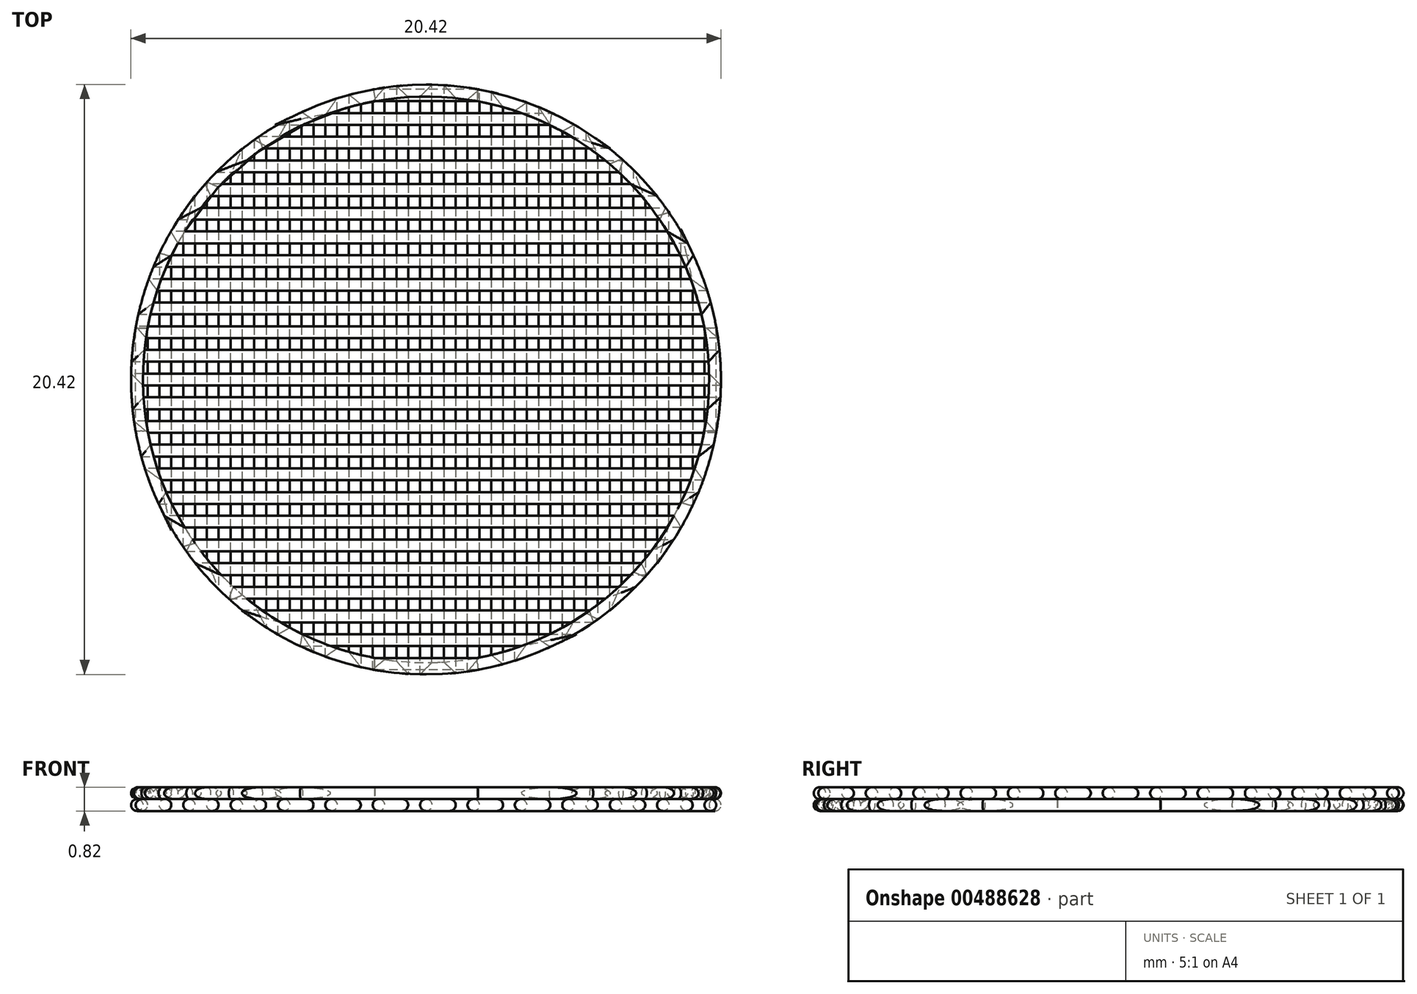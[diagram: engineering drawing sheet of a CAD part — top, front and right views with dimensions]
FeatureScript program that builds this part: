
annotation { "Feature Type Name" : "Feature", "Feature Type Description" : "" }
export const myFeature = defineFeature(function(context is Context, id is Id, definition is map)
    precondition{}
    {
        {
            assignVariable(context, id + "F0", {"name" : "d", "anyValue" : 0.4 * mm});
        }
        {
            var Q0;
            Q0=qCreatedBy(makeId("Top.planeOp"),FACE);
            cPlane(context, id + "F1", {"entities" : qUnion([Q0]), "cplaneType" : CPlaneType.OFFSET, "offset" : getVariable(context, 'd') / 2, "width" : 150 * mm, "height" : 150 * mm});
        }
        {
            var Q0;
            Q0=qCreatedBy(id+"F1.planeOp",FACE);
            var sketch = newSketch(context, id + "F2", { "sketchPlane" : qUnion([Q0])});
            skLineSegment(sketch, "E0.bottom", {"start": v(10, 10) * mm, "end": v(-10, 10) * mm});
            skLineSegment(sketch, "E0.top", {"start": v(10, -10) * mm, "end": v(-10, -10) * mm});
            skLineSegment(sketch, "E0.left", {"start": v(10, 10) * mm, "end": v(10, -10) * mm});
            skLineSegment(sketch, "E0.right", {"start": v(-10, 10) * mm, "end": v(-10, -10) * mm});
            skPoint(sketch, "E0.middle", {"position": v(0, 0) * mm});
            skLineSegment(sketch, "E1", {"start": v(10, -10) * mm, "end": v(9.84, -10) * mm});
            skLineSegment(sketch, "E2", {"start": v(9.84, -10) * mm, "end": v(9.02, -10) * mm});
            skLineSegment(sketch, "E3", {"start": v(9.02, -10) * mm, "end": v(8.2, -10) * mm});
            skLineSegment(sketch, "E4", {"start": v(8.2, -10) * mm, "end": v(7.38, -10) * mm});
            skLineSegment(sketch, "E5", {"start": v(7.38, -10) * mm, "end": v(6.56, -10) * mm});
            skLineSegment(sketch, "E6", {"start": v(6.56, -10) * mm, "end": v(5.74, -10) * mm});
            skLineSegment(sketch, "E7", {"start": v(5.74, -10) * mm, "end": v(4.92, -10) * mm});
            skLineSegment(sketch, "E8", {"start": v(4.92, -10) * mm, "end": v(4.1, -10) * mm});
            skLineSegment(sketch, "E9", {"start": v(4.1, -10) * mm, "end": v(3.28, -10) * mm});
            skLineSegment(sketch, "E10", {"start": v(3.28, -10) * mm, "end": v(2.46, -10) * mm});
            skLineSegment(sketch, "E11", {"start": v(2.46, -10) * mm, "end": v(1.64, -10) * mm});
            skLineSegment(sketch, "E12", {"start": v(1.64, -10) * mm, "end": v(0.82, -10) * mm});
            skLineSegment(sketch, "E13", {"start": v(0.82, -10) * mm, "end": v(0, -10) * mm});
            skLineSegment(sketch, "E14", {"start": v(0, -10) * mm, "end": v(-0.82, -10) * mm});
            skLineSegment(sketch, "E15", {"start": v(-0.82, -10) * mm, "end": v(-1.64, -10) * mm});
            skLineSegment(sketch, "E16", {"start": v(-1.64, -10) * mm, "end": v(-2.46, -10) * mm});
            skLineSegment(sketch, "E17", {"start": v(-2.46, -10) * mm, "end": v(-3.28, -10) * mm});
            skLineSegment(sketch, "E18", {"start": v(-3.28, -10) * mm, "end": v(-4.1, -10) * mm});
            skLineSegment(sketch, "E19", {"start": v(-4.1, -10) * mm, "end": v(-4.92, -10) * mm});
            skLineSegment(sketch, "E20", {"start": v(-4.92, -10) * mm, "end": v(-5.74, -10) * mm});
            skLineSegment(sketch, "E21", {"start": v(-5.74, -10) * mm, "end": v(-6.56, -10) * mm});
            skLineSegment(sketch, "E22", {"start": v(-6.56, -10) * mm, "end": v(-7.38, -10) * mm});
            skLineSegment(sketch, "E23", {"start": v(-7.38, -10) * mm, "end": v(-8.2, -10) * mm});
            skLineSegment(sketch, "E24", {"start": v(-8.2, -10) * mm, "end": v(-9.02, -10) * mm});
            skLineSegment(sketch, "E25", {"start": v(-9.02, -10) * mm, "end": v(-9.84, -10) * mm});
            skLineSegment(sketch, "E26", {"start": v(-9.84, -10) * mm, "end": v(-10, -10) * mm});
            skLineSegment(sketch, "E27", {"start": v(9.84, -10) * mm, "end": v(9.84, -1.78) * mm});
            skLineSegment(sketch, "E28", {"start": v(9.84, -1.78) * mm, "end": v(9.84, 1.78) * mm});
            skLineSegment(sketch, "E29", {"start": v(9.84, 1.78) * mm, "end": v(9.84, 10) * mm});
            skLineSegment(sketch, "E30", {"start": v(9.84, 10) * mm, "end": v(10, 10) * mm});
            skLineSegment(sketch, "E31", {"start": v(9.02, -10) * mm, "end": v(9.02, -4.32) * mm});
            skLineSegment(sketch, "E32", {"start": v(9.02, -4.32) * mm, "end": v(9.02, 4.32) * mm});
            skLineSegment(sketch, "E33", {"start": v(9.02, 4.32) * mm, "end": v(9.02, 10) * mm});
            skLineSegment(sketch, "E34", {"start": v(9.02, 10) * mm, "end": v(9.84, 10) * mm});
            skLineSegment(sketch, "E35", {"start": v(8.2, -10) * mm, "end": v(8.2, -5.72) * mm});
            skLineSegment(sketch, "E36", {"start": v(8.2, -5.72) * mm, "end": v(8.2, 5.72) * mm});
            skLineSegment(sketch, "E37", {"start": v(8.2, 5.72) * mm, "end": v(8.2, 10) * mm});
            skLineSegment(sketch, "E38", {"start": v(8.2, 10) * mm, "end": v(9.02, 10) * mm});
            skLineSegment(sketch, "E39", {"start": v(7.38, -10) * mm, "end": v(7.38, -6.75) * mm});
            skLineSegment(sketch, "E40", {"start": v(7.38, -6.75) * mm, "end": v(7.38, 6.75) * mm});
            skLineSegment(sketch, "E41", {"start": v(7.38, 6.75) * mm, "end": v(7.38, 10) * mm});
            skLineSegment(sketch, "E42", {"start": v(7.38, 10) * mm, "end": v(8.2, 10) * mm});
            skLineSegment(sketch, "E43", {"start": v(6.56, -10) * mm, "end": v(6.56, -7.55) * mm});
            skLineSegment(sketch, "E44", {"start": v(6.56, -7.55) * mm, "end": v(6.56, 7.55) * mm});
            skLineSegment(sketch, "E45", {"start": v(6.56, 7.55) * mm, "end": v(6.56, 10) * mm});
            skLineSegment(sketch, "E46", {"start": v(6.56, 10) * mm, "end": v(7.38, 10) * mm});
            skLineSegment(sketch, "E47", {"start": v(5.74, -10) * mm, "end": v(5.74, -8.19) * mm});
            skLineSegment(sketch, "E48", {"start": v(5.74, -8.19) * mm, "end": v(5.74, 8.19) * mm});
            skLineSegment(sketch, "E49", {"start": v(5.74, 8.19) * mm, "end": v(5.74, 10) * mm});
            skLineSegment(sketch, "E50", {"start": v(5.74, 10) * mm, "end": v(6.56, 10) * mm});
            skLineSegment(sketch, "E51", {"start": v(4.92, -10) * mm, "end": v(4.92, -8.7) * mm});
            skLineSegment(sketch, "E52", {"start": v(4.92, -8.7) * mm, "end": v(4.92, 8.7) * mm});
            skLineSegment(sketch, "E53", {"start": v(4.92, 8.7) * mm, "end": v(4.92, 10) * mm});
            skLineSegment(sketch, "E54", {"start": v(4.92, 10) * mm, "end": v(5.74, 10) * mm});
            skLineSegment(sketch, "E55", {"start": v(4.1, -10) * mm, "end": v(4.1, -9.12) * mm});
            skLineSegment(sketch, "E56", {"start": v(4.1, -9.12) * mm, "end": v(4.1, 9.12) * mm});
            skLineSegment(sketch, "E57", {"start": v(4.1, 9.12) * mm, "end": v(4.1, 10) * mm});
            skLineSegment(sketch, "E58", {"start": v(4.1, 10) * mm, "end": v(4.92, 10) * mm});
            skLineSegment(sketch, "E59", {"start": v(3.28, -10) * mm, "end": v(3.28, -9.45) * mm});
            skLineSegment(sketch, "E60", {"start": v(3.28, -9.45) * mm, "end": v(3.28, 9.45) * mm});
            skLineSegment(sketch, "E61", {"start": v(3.28, 9.45) * mm, "end": v(3.28, 10) * mm});
            skLineSegment(sketch, "E62", {"start": v(3.28, 10) * mm, "end": v(4.1, 10) * mm});
            skLineSegment(sketch, "E63", {"start": v(2.46, -10) * mm, "end": v(2.46, -9.7) * mm});
            skLineSegment(sketch, "E64", {"start": v(2.46, -9.7) * mm, "end": v(2.46, 9.7) * mm});
            skLineSegment(sketch, "E65", {"start": v(2.46, 9.7) * mm, "end": v(2.46, 10) * mm});
            skLineSegment(sketch, "E66", {"start": v(2.46, 10) * mm, "end": v(3.28, 10) * mm});
            skLineSegment(sketch, "E67", {"start": v(1.64, -10) * mm, "end": v(1.64, -9.86) * mm});
            skLineSegment(sketch, "E68", {"start": v(1.64, -9.86) * mm, "end": v(1.64, 9.86) * mm});
            skLineSegment(sketch, "E69", {"start": v(1.64, 9.86) * mm, "end": v(1.64, 10) * mm});
            skLineSegment(sketch, "E70", {"start": v(1.64, 10) * mm, "end": v(2.46, 10) * mm});
            skLineSegment(sketch, "E71", {"start": v(0.82, -10) * mm, "end": v(0.82, -9.97) * mm});
            skLineSegment(sketch, "E72", {"start": v(0.82, -9.97) * mm, "end": v(0.82, 9.97) * mm});
            skLineSegment(sketch, "E73", {"start": v(0.82, 9.97) * mm, "end": v(0.82, 10) * mm});
            skLineSegment(sketch, "E74", {"start": v(0.82, 10) * mm, "end": v(1.64, 10) * mm});
            skLineSegment(sketch, "E75", {"start": v(0, -10) * mm, "end": v(0, 10) * mm});
            skLineSegment(sketch, "E76", {"start": v(0, 10) * mm, "end": v(0.82, 10) * mm});
            skLineSegment(sketch, "E77", {"start": v(-0.82, -10) * mm, "end": v(-0.82, -9.97) * mm});
            skLineSegment(sketch, "E78", {"start": v(-0.82, -9.97) * mm, "end": v(-0.82, 9.97) * mm});
            skLineSegment(sketch, "E79", {"start": v(-0.82, 9.97) * mm, "end": v(-0.82, 10) * mm});
            skLineSegment(sketch, "E80", {"start": v(-0.82, 10) * mm, "end": v(0, 10) * mm});
            skLineSegment(sketch, "E81", {"start": v(-1.64, -10) * mm, "end": v(-1.64, -9.86) * mm});
            skLineSegment(sketch, "E82", {"start": v(-1.64, -9.86) * mm, "end": v(-1.64, 9.86) * mm});
            skLineSegment(sketch, "E83", {"start": v(-1.64, 9.86) * mm, "end": v(-1.64, 10) * mm});
            skLineSegment(sketch, "E84", {"start": v(-1.64, 10) * mm, "end": v(-0.82, 10) * mm});
            skLineSegment(sketch, "E85", {"start": v(-2.46, -10) * mm, "end": v(-2.46, -9.7) * mm});
            skLineSegment(sketch, "E86", {"start": v(-2.46, -9.7) * mm, "end": v(-2.46, 9.7) * mm});
            skLineSegment(sketch, "E87", {"start": v(-2.46, 9.7) * mm, "end": v(-2.46, 10) * mm});
            skLineSegment(sketch, "E88", {"start": v(-2.46, 10) * mm, "end": v(-1.64, 10) * mm});
            skLineSegment(sketch, "E89", {"start": v(-3.28, -10) * mm, "end": v(-3.28, -9.45) * mm});
            skLineSegment(sketch, "E90", {"start": v(-3.28, -9.45) * mm, "end": v(-3.28, 9.45) * mm});
            skLineSegment(sketch, "E91", {"start": v(-3.28, 9.45) * mm, "end": v(-3.28, 10) * mm});
            skLineSegment(sketch, "E92", {"start": v(-3.28, 10) * mm, "end": v(-2.46, 10) * mm});
            skLineSegment(sketch, "E93", {"start": v(-4.1, -10) * mm, "end": v(-4.1, -9.12) * mm});
            skLineSegment(sketch, "E94", {"start": v(-4.1, -9.12) * mm, "end": v(-4.1, 9.12) * mm});
            skLineSegment(sketch, "E95", {"start": v(-4.1, 9.12) * mm, "end": v(-4.1, 10) * mm});
            skLineSegment(sketch, "E96", {"start": v(-4.1, 10) * mm, "end": v(-3.28, 10) * mm});
            skLineSegment(sketch, "E97", {"start": v(-4.92, -10) * mm, "end": v(-4.92, -8.7) * mm});
            skLineSegment(sketch, "E98", {"start": v(-4.92, -8.7) * mm, "end": v(-4.92, 8.7) * mm});
            skLineSegment(sketch, "E99", {"start": v(-4.92, 8.7) * mm, "end": v(-4.92, 10) * mm});
            skLineSegment(sketch, "E100", {"start": v(-4.92, 10) * mm, "end": v(-4.1, 10) * mm});
            skLineSegment(sketch, "E101", {"start": v(-5.74, -10) * mm, "end": v(-5.74, -8.19) * mm});
            skLineSegment(sketch, "E102", {"start": v(-5.74, -8.19) * mm, "end": v(-5.74, 8.19) * mm});
            skLineSegment(sketch, "E103", {"start": v(-5.74, 8.19) * mm, "end": v(-5.74, 10) * mm});
            skLineSegment(sketch, "E104", {"start": v(-5.74, 10) * mm, "end": v(-4.92, 10) * mm});
            skLineSegment(sketch, "E105", {"start": v(-6.56, -10) * mm, "end": v(-6.56, -7.55) * mm});
            skLineSegment(sketch, "E106", {"start": v(-6.56, -7.55) * mm, "end": v(-6.56, 7.55) * mm});
            skLineSegment(sketch, "E107", {"start": v(-6.56, 7.55) * mm, "end": v(-6.56, 10) * mm});
            skLineSegment(sketch, "E108", {"start": v(-6.56, 10) * mm, "end": v(-5.74, 10) * mm});
            skLineSegment(sketch, "E109", {"start": v(-7.38, -10) * mm, "end": v(-7.38, -6.75) * mm});
            skLineSegment(sketch, "E110", {"start": v(-7.38, -6.75) * mm, "end": v(-7.38, 6.75) * mm});
            skLineSegment(sketch, "E111", {"start": v(-7.38, 6.75) * mm, "end": v(-7.38, 10) * mm});
            skLineSegment(sketch, "E112", {"start": v(-7.38, 10) * mm, "end": v(-6.56, 10) * mm});
            skLineSegment(sketch, "E113", {"start": v(-8.2, -10) * mm, "end": v(-8.2, -5.72) * mm});
            skLineSegment(sketch, "E114", {"start": v(-8.2, -5.72) * mm, "end": v(-8.2, 5.72) * mm});
            skLineSegment(sketch, "E115", {"start": v(-8.2, 5.72) * mm, "end": v(-8.2, 10) * mm});
            skLineSegment(sketch, "E116", {"start": v(-8.2, 10) * mm, "end": v(-7.38, 10) * mm});
            skLineSegment(sketch, "E117", {"start": v(-9.02, -10) * mm, "end": v(-9.02, -4.32) * mm});
            skLineSegment(sketch, "E118", {"start": v(-9.02, -4.32) * mm, "end": v(-9.02, 4.32) * mm});
            skLineSegment(sketch, "E119", {"start": v(-9.02, 4.32) * mm, "end": v(-9.02, 10) * mm});
            skLineSegment(sketch, "E120", {"start": v(-9.02, 10) * mm, "end": v(-8.2, 10) * mm});
            skLineSegment(sketch, "E121", {"start": v(-9.84, -10) * mm, "end": v(-9.84, -1.78) * mm});
            skLineSegment(sketch, "E122", {"start": v(-9.84, -1.78) * mm, "end": v(-9.84, 1.78) * mm});
            skLineSegment(sketch, "E123", {"start": v(-9.84, 1.78) * mm, "end": v(-9.84, 10) * mm});
            skLineSegment(sketch, "E124", {"start": v(-9.84, 10) * mm, "end": v(-9.02, 10) * mm});
            skLineSegment(sketch, "E125", {"start": v(-10, 10) * mm, "end": v(-9.84, 10) * mm});
            skArc(sketch, "E126", {"start": v(9.84, 1.78) * mm, "mid": v(9.51, 3.08) * mm, "end": v(9.02, 4.32) * mm});
            skArc(sketch, "E127", {"start": v(8.2, 5.72) * mm, "mid": v(7.8, 6.25) * mm, "end": v(7.38, 6.75) * mm});
            skArc(sketch, "E128", {"start": v(6.56, 7.55) * mm, "mid": v(6.16, 7.88) * mm, "end": v(5.74, 8.19) * mm});
            skArc(sketch, "E129", {"start": v(4.92, 8.7) * mm, "mid": v(4.51, 8.92) * mm, "end": v(4.1, 9.12) * mm});
            skArc(sketch, "E130", {"start": v(3.28, 9.45) * mm, "mid": v(2.87, 9.58) * mm, "end": v(2.46, 9.7) * mm});
            skArc(sketch, "E131", {"start": v(1.64, 9.86) * mm, "mid": v(1.23, 9.92) * mm, "end": v(0.82, 9.97) * mm});
            skArc(sketch, "E132", {"start": v(0, 10) * mm, "mid": v(-0.41, 10) * mm, "end": v(-0.82, 9.97) * mm});
            skArc(sketch, "E133", {"start": v(-2.46, 9.7) * mm, "mid": v(-2.87, 9.58) * mm, "end": v(-3.28, 9.45) * mm});
            skArc(sketch, "E134", {"start": v(-4.1, 9.12) * mm, "mid": v(-4.51, 8.92) * mm, "end": v(-4.92, 8.7) * mm});
            skArc(sketch, "E135", {"start": v(-5.74, 8.19) * mm, "mid": v(-6.16, 7.88) * mm, "end": v(-6.56, 7.55) * mm});
            skArc(sketch, "E136", {"start": v(-7.38, 6.75) * mm, "mid": v(-7.8, 6.25) * mm, "end": v(-8.2, 5.72) * mm});
            skArc(sketch, "E137", {"start": v(-9.02, 4.32) * mm, "mid": v(-9.51, 3.08) * mm, "end": v(-9.84, 1.78) * mm});
            skArc(sketch, "E138", {"start": v(-9.84, -1.78) * mm, "mid": v(-9.51, -3.08) * mm, "end": v(-9.02, -4.32) * mm});
            skArc(sketch, "E139", {"start": v(-8.2, -5.72) * mm, "mid": v(-7.8, -6.25) * mm, "end": v(-7.38, -6.75) * mm});
            skArc(sketch, "E140", {"start": v(-6.56, -7.55) * mm, "mid": v(-6.16, -7.88) * mm, "end": v(-5.74, -8.19) * mm});
            skArc(sketch, "E141", {"start": v(-4.92, -8.7) * mm, "mid": v(-4.51, -8.92) * mm, "end": v(-4.1, -9.12) * mm});
            skArc(sketch, "E142", {"start": v(-3.28, -9.45) * mm, "mid": v(-2.87, -9.58) * mm, "end": v(-2.46, -9.7) * mm});
            skArc(sketch, "E143", {"start": v(-1.64, -9.86) * mm, "mid": v(-1.23, -9.92) * mm, "end": v(-0.82, -9.97) * mm});
            skArc(sketch, "E144", {"start": v(0, -10) * mm, "mid": v(0.41, -10) * mm, "end": v(0.82, -9.97) * mm});
            skArc(sketch, "E145", {"start": v(1.64, -9.86) * mm, "mid": v(2.05, -9.79) * mm, "end": v(2.46, -9.7) * mm});
            skArc(sketch, "E146", {"start": v(3.28, -9.45) * mm, "mid": v(3.7, -9.3) * mm, "end": v(4.1, -9.12) * mm});
            skArc(sketch, "E147", {"start": v(4.92, -8.7) * mm, "mid": v(5.34, -8.46) * mm, "end": v(5.74, -8.19) * mm});
            skArc(sketch, "E148", {"start": v(6.56, -7.55) * mm, "mid": v(6.98, -7.16) * mm, "end": v(7.38, -6.75) * mm});
            skArc(sketch, "E149", {"start": v(8.2, -5.72) * mm, "mid": v(8.64, -5.04) * mm, "end": v(9.02, -4.32) * mm});
            skCircle(sketch, "E150", {"center": v(0, 0) * mm, "radius": 10 * mm});
            skArc(sketch, "E151", {"start": v(-9.02, 4.32) * mm, "mid": v(-8.64, 5.04) * mm, "end": v(-8.2, 5.72) * mm});
            skArc(sketch, "E152", {"start": v(-7.38, 6.75) * mm, "mid": v(-6.98, 7.16) * mm, "end": v(-6.56, 7.55) * mm});
            skArc(sketch, "E153", {"start": v(-5.74, 8.19) * mm, "mid": v(-5.34, 8.46) * mm, "end": v(-4.92, 8.7) * mm});
            skArc(sketch, "E154", {"start": v(-4.1, 9.12) * mm, "mid": v(-3.7, 9.3) * mm, "end": v(-3.28, 9.45) * mm});
            skArc(sketch, "E155", {"start": v(-2.46, 9.7) * mm, "mid": v(-2.05, 9.79) * mm, "end": v(-1.64, 9.86) * mm});
            skSolve(sketch);
        }
        {
            var Q0;
            Q0=qCreatedBy(makeId("Front.planeOp"),FACE);
            var sketch = newSketch(context, id + "F3", { "sketchPlane" : qUnion([Q0])});
            skCircle(sketch, "E156", {"center": v(-10, 0.2) * mm, "radius": 0.2 * mm});
            skSolve(sketch);
        }
        {
            var Q0;
            Q0=makeQuery(id+"F3.imprint","IMPRINT",FACE,{"disambiguationData":[TD([[makeQuery(id+"F3.imprint","IMPRINT",EDGE,{"derivedFrom":sQuery(id+"F3.wireOp",EDGE,"E156")}),1.0]])]});
            var Q1;
            Q1=sQuery(id+"F3.wireOp",EDGE,"E156");
            var Q2;
            Q2=sQuery(id+"F2.wireOp",EDGE,"E150");
            sweep(context, id + "F4", {"profiles" : qUnion([Q0]), "surfaceProfiles" : qUnion([Q1]), "path" : qUnion([Q2])});
        }
        {
            var Q0;
            Q0=sQuery(id+"F2.wireOp",EDGE,"E28");
            var Q1;
            Q1=sQuery(id+"F2.wireOp",VERTEX,"E28.start");
            cPlane(context, id + "F5", {"entities" : qUnion([Q0, Q1]), "cplaneType" : CPlaneType.LINE_POINT, "offset" : 25 * mm, "width" : 150 * mm, "height" : 150 * mm});
        }
        {
            var Q0;
            Q0=qCreatedBy(id+"F5.planeOp",FACE);
            var sketch = newSketch(context, id + "F6", { "sketchPlane" : qUnion([Q0])});
            skCircle(sketch, "E157", {"center": v(-9.84, 0.2) * mm, "radius": 0.2 * mm});
            skSolve(sketch);
        }
        {
            var Q0;
            Q0 = qSketchRegion(id + "F6", true);
            var Q1;
            Q1=sQuery(id+"F2.wireOp",EDGE,"E130");
            var Q2;
            Q2=sQuery(id+"F2.wireOp",EDGE,"E129");
            var Q3;
            Q3=sQuery(id+"F2.wireOp",EDGE,"E127");
            var Q4;
            Q4=sQuery(id+"F2.wireOp",EDGE,"E128");
            var Q5;
            Q5=sQuery(id+"F2.wireOp",EDGE,"E126");
            var Q6;
            Q6=sQuery(id+"F2.wireOp",EDGE,"E149");
            var Q7;
            Q7=sQuery(id+"F2.wireOp",EDGE,"E148");
            var Q8;
            Q8=sQuery(id+"F2.wireOp",EDGE,"E147");
            var Q9;
            Q9=sQuery(id+"F2.wireOp",EDGE,"E146");
            var Q10;
            Q10=sQuery(id+"F2.wireOp",EDGE,"E145");
            var Q11;
            Q11=sQuery(id+"F2.wireOp",EDGE,"E144");
            var Q12;
            Q12=sQuery(id+"F2.wireOp",EDGE,"E143");
            var Q13;
            Q13=sQuery(id+"F2.wireOp",EDGE,"E142");
            var Q14;
            Q14=sQuery(id+"F2.wireOp",EDGE,"E141");
            var Q15;
            Q15=sQuery(id+"F2.wireOp",EDGE,"E140");
            var Q16;
            Q16=sQuery(id+"F2.wireOp",EDGE,"E139");
            var Q17;
            Q17=sQuery(id+"F2.wireOp",EDGE,"E138");
            var Q18;
            Q18=sQuery(id+"F2.wireOp",EDGE,"E28");
            var Q19;
            Q19=sQuery(id+"F2.wireOp",EDGE,"E32");
            var Q20;
            Q20=sQuery(id+"F2.wireOp",EDGE,"E36");
            var Q21;
            Q21=sQuery(id+"F2.wireOp",EDGE,"E40");
            var Q22;
            Q22=sQuery(id+"F2.wireOp",EDGE,"E44");
            var Q23;
            Q23=sQuery(id+"F2.wireOp",EDGE,"E48");
            var Q24;
            Q24=sQuery(id+"F2.wireOp",EDGE,"E52");
            var Q25;
            Q25=sQuery(id+"F2.wireOp",EDGE,"E56");
            var Q26;
            Q26=sQuery(id+"F2.wireOp",EDGE,"E60");
            var Q27;
            Q27=sQuery(id+"F2.wireOp",EDGE,"E64");
            var Q28;
            Q28=sQuery(id+"F2.wireOp",EDGE,"E68");
            var Q29;
            Q29=sQuery(id+"F2.wireOp",EDGE,"E131");
            var Q30;
            Q30=sQuery(id+"F2.wireOp",EDGE,"E72");
            var Q31;
            Q31=sQuery(id+"F2.wireOp",EDGE,"E75");
            var Q32;
            Q32=sQuery(id+"F2.wireOp",EDGE,"E132");
            var Q33;
            Q33=sQuery(id+"F2.wireOp",EDGE,"E78");
            var Q34;
            Q34=sQuery(id+"F2.wireOp",EDGE,"E82");
            var Q35;
            Q35=sQuery(id+"F2.wireOp",EDGE,"E86");
            var Q36;
            Q36=sQuery(id+"F2.wireOp",EDGE,"E90");
            var Q37;
            Q37=sQuery(id+"F2.wireOp",EDGE,"E94");
            var Q38;
            Q38=sQuery(id+"F2.wireOp",EDGE,"E98");
            var Q39;
            Q39=sQuery(id+"F2.wireOp",EDGE,"E102");
            var Q40;
            Q40=sQuery(id+"F2.wireOp",EDGE,"E106");
            var Q41;
            Q41=sQuery(id+"F2.wireOp",EDGE,"E110");
            var Q42;
            Q42=sQuery(id+"F2.wireOp",EDGE,"E114");
            var Q43;
            Q43=sQuery(id+"F2.wireOp",EDGE,"E118");
            var Q44;
            Q44=sQuery(id+"F2.wireOp",EDGE,"E122");
            var Q45;
            Q45=sQuery(id+"F2.wireOp",EDGE,"E151");
            var Q46;
            Q46=sQuery(id+"F2.wireOp",EDGE,"E152");
            var Q47;
            Q47=sQuery(id+"F2.wireOp",EDGE,"E153");
            var Q48;
            Q48=sQuery(id+"F2.wireOp",EDGE,"E154");
            var Q49;
            Q49=sQuery(id+"F2.wireOp",EDGE,"E155");
            sweep(context, id + "F7", {"profiles" : qUnion([Q0]), "path" : qUnion([Q1, Q2, Q3, Q4, Q5, Q6, Q7, Q8, Q9, Q10, Q11, Q12, Q13, Q14, Q15, Q16, Q17, Q18, Q19, Q20, Q21, Q22, Q23, Q24, Q25, Q26, Q27, Q28, Q29, Q30, Q31, Q32, Q33, Q34, Q35, Q36, Q37, Q38, Q39, Q40, Q41, Q42, Q43, Q44, Q45, Q46, Q47, Q48, Q49])});
        }
        {
            var Q0;
            Q0=qCreatedBy(id+"F1.planeOp",FACE);
            cPlane(context, id + "F8", {"entities" : qUnion([Q0]), "cplaneType" : CPlaneType.OFFSET, "offset" : getVariable(context, 'd'), "width" : 150 * mm, "height" : 150 * mm});
        }
        {
            var Q0;
            Q0=qCreatedBy(id+"F8.planeOp",FACE);
            var sketch = newSketch(context, id + "F9", { "sketchPlane" : qUnion([Q0])});
            skLineSegment(sketch, "E158.bottom", {"start": v(-10, 10) * mm, "end": v(-10, -10) * mm});
            skLineSegment(sketch, "E158.top", {"start": v(10, 10) * mm, "end": v(10, -10) * mm});
            skLineSegment(sketch, "E158.left", {"start": v(-10, 10) * mm, "end": v(10, 10) * mm});
            skLineSegment(sketch, "E158.right", {"start": v(-10, -10) * mm, "end": v(10, -10) * mm});
            skPoint(sketch, "E158.middle", {"position": v(0, 0) * mm});
            skLineSegment(sketch, "E159", {"start": v(10, 10) * mm, "end": v(10, 9.84) * mm});
            skLineSegment(sketch, "E160", {"start": v(10, 9.84) * mm, "end": v(10, 9.02) * mm});
            skLineSegment(sketch, "E161", {"start": v(10, 9.02) * mm, "end": v(10, 8.2) * mm});
            skLineSegment(sketch, "E162", {"start": v(10, 8.2) * mm, "end": v(10, 7.38) * mm});
            skLineSegment(sketch, "E163", {"start": v(10, 7.38) * mm, "end": v(10, 6.56) * mm});
            skLineSegment(sketch, "E164", {"start": v(10, 6.56) * mm, "end": v(10, 5.74) * mm});
            skLineSegment(sketch, "E165", {"start": v(10, 5.74) * mm, "end": v(10, 4.92) * mm});
            skLineSegment(sketch, "E166", {"start": v(10, 4.92) * mm, "end": v(10, 4.1) * mm});
            skLineSegment(sketch, "E167", {"start": v(10, 4.1) * mm, "end": v(10, 3.28) * mm});
            skLineSegment(sketch, "E168", {"start": v(10, 3.28) * mm, "end": v(10, 2.46) * mm});
            skLineSegment(sketch, "E169", {"start": v(10, 2.46) * mm, "end": v(10, 1.64) * mm});
            skLineSegment(sketch, "E170", {"start": v(10, 1.64) * mm, "end": v(10, 0.82) * mm});
            skLineSegment(sketch, "E171", {"start": v(10, 0.82) * mm, "end": v(10, 0) * mm});
            skLineSegment(sketch, "E172", {"start": v(10, 0) * mm, "end": v(10, -0.82) * mm});
            skLineSegment(sketch, "E173", {"start": v(10, -0.82) * mm, "end": v(10, -1.64) * mm});
            skLineSegment(sketch, "E174", {"start": v(10, -1.64) * mm, "end": v(10, -2.46) * mm});
            skLineSegment(sketch, "E175", {"start": v(10, -2.46) * mm, "end": v(10, -3.28) * mm});
            skLineSegment(sketch, "E176", {"start": v(10, -3.28) * mm, "end": v(10, -4.1) * mm});
            skLineSegment(sketch, "E177", {"start": v(10, -4.1) * mm, "end": v(10, -4.92) * mm});
            skLineSegment(sketch, "E178", {"start": v(10, -4.92) * mm, "end": v(10, -5.74) * mm});
            skLineSegment(sketch, "E179", {"start": v(10, -5.74) * mm, "end": v(10, -6.56) * mm});
            skLineSegment(sketch, "E180", {"start": v(10, -6.56) * mm, "end": v(10, -7.38) * mm});
            skLineSegment(sketch, "E181", {"start": v(10, -7.38) * mm, "end": v(10, -8.2) * mm});
            skLineSegment(sketch, "E182", {"start": v(10, -8.2) * mm, "end": v(10, -9.02) * mm});
            skLineSegment(sketch, "E183", {"start": v(10, -9.02) * mm, "end": v(10, -9.84) * mm});
            skLineSegment(sketch, "E184", {"start": v(10, -9.84) * mm, "end": v(10, -10) * mm});
            skLineSegment(sketch, "E185", {"start": v(10, 9.84) * mm, "end": v(1.78, 9.84) * mm});
            skLineSegment(sketch, "E186", {"start": v(1.78, 9.84) * mm, "end": v(-1.78, 9.84) * mm});
            skLineSegment(sketch, "E187", {"start": v(-1.78, 9.84) * mm, "end": v(-10, 9.84) * mm});
            skLineSegment(sketch, "E188", {"start": v(-10, 9.84) * mm, "end": v(-10, 10) * mm});
            skLineSegment(sketch, "E189", {"start": v(10, 9.02) * mm, "end": v(4.32, 9.02) * mm});
            skLineSegment(sketch, "E190", {"start": v(4.32, 9.02) * mm, "end": v(-4.32, 9.02) * mm});
            skLineSegment(sketch, "E191", {"start": v(-4.32, 9.02) * mm, "end": v(-10, 9.02) * mm});
            skLineSegment(sketch, "E192", {"start": v(-10, 9.02) * mm, "end": v(-10, 9.84) * mm});
            skLineSegment(sketch, "E193", {"start": v(10, 8.2) * mm, "end": v(5.72, 8.2) * mm});
            skLineSegment(sketch, "E194", {"start": v(5.72, 8.2) * mm, "end": v(-5.72, 8.2) * mm});
            skLineSegment(sketch, "E195", {"start": v(-5.72, 8.2) * mm, "end": v(-10, 8.2) * mm});
            skLineSegment(sketch, "E196", {"start": v(-10, 8.2) * mm, "end": v(-10, 9.02) * mm});
            skLineSegment(sketch, "E197", {"start": v(10, 7.38) * mm, "end": v(6.75, 7.38) * mm});
            skLineSegment(sketch, "E198", {"start": v(6.75, 7.38) * mm, "end": v(-6.75, 7.38) * mm});
            skLineSegment(sketch, "E199", {"start": v(-6.75, 7.38) * mm, "end": v(-10, 7.38) * mm});
            skLineSegment(sketch, "E200", {"start": v(-10, 7.38) * mm, "end": v(-10, 8.2) * mm});
            skLineSegment(sketch, "E201", {"start": v(10, 6.56) * mm, "end": v(7.55, 6.56) * mm});
            skLineSegment(sketch, "E202", {"start": v(7.55, 6.56) * mm, "end": v(-7.55, 6.56) * mm});
            skLineSegment(sketch, "E203", {"start": v(-7.55, 6.56) * mm, "end": v(-10, 6.56) * mm});
            skLineSegment(sketch, "E204", {"start": v(-10, 6.56) * mm, "end": v(-10, 7.38) * mm});
            skLineSegment(sketch, "E205", {"start": v(10, 5.74) * mm, "end": v(8.19, 5.74) * mm});
            skLineSegment(sketch, "E206", {"start": v(8.19, 5.74) * mm, "end": v(-8.19, 5.74) * mm});
            skLineSegment(sketch, "E207", {"start": v(-8.19, 5.74) * mm, "end": v(-10, 5.74) * mm});
            skLineSegment(sketch, "E208", {"start": v(-10, 5.74) * mm, "end": v(-10, 6.56) * mm});
            skLineSegment(sketch, "E209", {"start": v(10, 4.92) * mm, "end": v(8.7, 4.92) * mm});
            skLineSegment(sketch, "E210", {"start": v(8.7, 4.92) * mm, "end": v(-8.7, 4.92) * mm});
            skLineSegment(sketch, "E211", {"start": v(-8.7, 4.92) * mm, "end": v(-10, 4.92) * mm});
            skLineSegment(sketch, "E212", {"start": v(-10, 4.92) * mm, "end": v(-10, 5.74) * mm});
            skLineSegment(sketch, "E213", {"start": v(10, 4.1) * mm, "end": v(9.12, 4.1) * mm});
            skLineSegment(sketch, "E214", {"start": v(9.12, 4.1) * mm, "end": v(-9.12, 4.1) * mm});
            skLineSegment(sketch, "E215", {"start": v(-9.12, 4.1) * mm, "end": v(-10, 4.1) * mm});
            skLineSegment(sketch, "E216", {"start": v(-10, 4.1) * mm, "end": v(-10, 4.92) * mm});
            skLineSegment(sketch, "E217", {"start": v(10, 3.28) * mm, "end": v(9.45, 3.28) * mm});
            skLineSegment(sketch, "E218", {"start": v(9.45, 3.28) * mm, "end": v(-9.45, 3.28) * mm});
            skLineSegment(sketch, "E219", {"start": v(-9.45, 3.28) * mm, "end": v(-10, 3.28) * mm});
            skLineSegment(sketch, "E220", {"start": v(-10, 3.28) * mm, "end": v(-10, 4.1) * mm});
            skLineSegment(sketch, "E221", {"start": v(10, 2.46) * mm, "end": v(9.7, 2.46) * mm});
            skLineSegment(sketch, "E222", {"start": v(9.7, 2.46) * mm, "end": v(-9.7, 2.46) * mm});
            skLineSegment(sketch, "E223", {"start": v(-9.7, 2.46) * mm, "end": v(-10, 2.46) * mm});
            skLineSegment(sketch, "E224", {"start": v(-10, 2.46) * mm, "end": v(-10, 3.28) * mm});
            skLineSegment(sketch, "E225", {"start": v(10, 1.64) * mm, "end": v(9.86, 1.64) * mm});
            skLineSegment(sketch, "E226", {"start": v(9.86, 1.64) * mm, "end": v(-9.86, 1.64) * mm});
            skLineSegment(sketch, "E227", {"start": v(-9.86, 1.64) * mm, "end": v(-10, 1.64) * mm});
            skLineSegment(sketch, "E228", {"start": v(-10, 1.64) * mm, "end": v(-10, 2.46) * mm});
            skLineSegment(sketch, "E229", {"start": v(10, 0.82) * mm, "end": v(9.97, 0.82) * mm});
            skLineSegment(sketch, "E230", {"start": v(9.97, 0.82) * mm, "end": v(-9.97, 0.82) * mm});
            skLineSegment(sketch, "E231", {"start": v(-9.97, 0.82) * mm, "end": v(-10, 0.82) * mm});
            skLineSegment(sketch, "E232", {"start": v(-10, 0.82) * mm, "end": v(-10, 1.64) * mm});
            skLineSegment(sketch, "E233", {"start": v(10, 0) * mm, "end": v(-10, 0) * mm});
            skLineSegment(sketch, "E234", {"start": v(-10, 0) * mm, "end": v(-10, 0.82) * mm});
            skLineSegment(sketch, "E235", {"start": v(10, -0.82) * mm, "end": v(9.97, -0.82) * mm});
            skLineSegment(sketch, "E236", {"start": v(9.97, -0.82) * mm, "end": v(-9.97, -0.82) * mm});
            skLineSegment(sketch, "E237", {"start": v(-9.97, -0.82) * mm, "end": v(-10, -0.82) * mm});
            skLineSegment(sketch, "E238", {"start": v(-10, -0.82) * mm, "end": v(-10, 0) * mm});
            skLineSegment(sketch, "E239", {"start": v(10, -1.64) * mm, "end": v(9.86, -1.64) * mm});
            skLineSegment(sketch, "E240", {"start": v(9.86, -1.64) * mm, "end": v(-9.86, -1.64) * mm});
            skLineSegment(sketch, "E241", {"start": v(-9.86, -1.64) * mm, "end": v(-10, -1.64) * mm});
            skLineSegment(sketch, "E242", {"start": v(-10, -1.64) * mm, "end": v(-10, -0.82) * mm});
            skLineSegment(sketch, "E243", {"start": v(10, -2.46) * mm, "end": v(9.7, -2.46) * mm});
            skLineSegment(sketch, "E244", {"start": v(9.7, -2.46) * mm, "end": v(-9.7, -2.46) * mm});
            skLineSegment(sketch, "E245", {"start": v(-9.7, -2.46) * mm, "end": v(-10, -2.46) * mm});
            skLineSegment(sketch, "E246", {"start": v(-10, -2.46) * mm, "end": v(-10, -1.64) * mm});
            skLineSegment(sketch, "E247", {"start": v(10, -3.28) * mm, "end": v(9.45, -3.28) * mm});
            skLineSegment(sketch, "E248", {"start": v(9.45, -3.28) * mm, "end": v(-9.45, -3.28) * mm});
            skLineSegment(sketch, "E249", {"start": v(-9.45, -3.28) * mm, "end": v(-10, -3.28) * mm});
            skLineSegment(sketch, "E250", {"start": v(-10, -3.28) * mm, "end": v(-10, -2.46) * mm});
            skLineSegment(sketch, "E251", {"start": v(10, -4.1) * mm, "end": v(9.12, -4.1) * mm});
            skLineSegment(sketch, "E252", {"start": v(9.12, -4.1) * mm, "end": v(-9.12, -4.1) * mm});
            skLineSegment(sketch, "E253", {"start": v(-9.12, -4.1) * mm, "end": v(-10, -4.1) * mm});
            skLineSegment(sketch, "E254", {"start": v(-10, -4.1) * mm, "end": v(-10, -3.28) * mm});
            skLineSegment(sketch, "E255", {"start": v(10, -4.92) * mm, "end": v(8.7, -4.92) * mm});
            skLineSegment(sketch, "E256", {"start": v(8.7, -4.92) * mm, "end": v(-8.7, -4.92) * mm});
            skLineSegment(sketch, "E257", {"start": v(-8.7, -4.92) * mm, "end": v(-10, -4.92) * mm});
            skLineSegment(sketch, "E258", {"start": v(-10, -4.92) * mm, "end": v(-10, -4.1) * mm});
            skLineSegment(sketch, "E259", {"start": v(10, -5.74) * mm, "end": v(8.19, -5.74) * mm});
            skLineSegment(sketch, "E260", {"start": v(8.19, -5.74) * mm, "end": v(-8.19, -5.74) * mm});
            skLineSegment(sketch, "E261", {"start": v(-8.19, -5.74) * mm, "end": v(-10, -5.74) * mm});
            skLineSegment(sketch, "E262", {"start": v(-10, -5.74) * mm, "end": v(-10, -4.92) * mm});
            skLineSegment(sketch, "E263", {"start": v(10, -6.56) * mm, "end": v(7.55, -6.56) * mm});
            skLineSegment(sketch, "E264", {"start": v(7.55, -6.56) * mm, "end": v(-7.55, -6.56) * mm});
            skLineSegment(sketch, "E265", {"start": v(-7.55, -6.56) * mm, "end": v(-10, -6.56) * mm});
            skLineSegment(sketch, "E266", {"start": v(-10, -6.56) * mm, "end": v(-10, -5.74) * mm});
            skLineSegment(sketch, "E267", {"start": v(10, -7.38) * mm, "end": v(6.75, -7.38) * mm});
            skLineSegment(sketch, "E268", {"start": v(6.75, -7.38) * mm, "end": v(-6.75, -7.38) * mm});
            skLineSegment(sketch, "E269", {"start": v(-6.75, -7.38) * mm, "end": v(-10, -7.38) * mm});
            skLineSegment(sketch, "E270", {"start": v(-10, -7.38) * mm, "end": v(-10, -6.56) * mm});
            skLineSegment(sketch, "E271", {"start": v(10, -8.2) * mm, "end": v(5.72, -8.2) * mm});
            skLineSegment(sketch, "E272", {"start": v(5.72, -8.2) * mm, "end": v(-5.72, -8.2) * mm});
            skLineSegment(sketch, "E273", {"start": v(-5.72, -8.2) * mm, "end": v(-10, -8.2) * mm});
            skLineSegment(sketch, "E274", {"start": v(-10, -8.2) * mm, "end": v(-10, -7.38) * mm});
            skLineSegment(sketch, "E275", {"start": v(10, -9.02) * mm, "end": v(4.32, -9.02) * mm});
            skLineSegment(sketch, "E276", {"start": v(4.32, -9.02) * mm, "end": v(-4.32, -9.02) * mm});
            skLineSegment(sketch, "E277", {"start": v(-4.32, -9.02) * mm, "end": v(-10, -9.02) * mm});
            skLineSegment(sketch, "E278", {"start": v(-10, -9.02) * mm, "end": v(-10, -8.2) * mm});
            skLineSegment(sketch, "E279", {"start": v(10, -9.84) * mm, "end": v(1.78, -9.84) * mm});
            skLineSegment(sketch, "E280", {"start": v(1.78, -9.84) * mm, "end": v(-1.78, -9.84) * mm});
            skLineSegment(sketch, "E281", {"start": v(-1.78, -9.84) * mm, "end": v(-10, -9.84) * mm});
            skLineSegment(sketch, "E282", {"start": v(-10, -9.84) * mm, "end": v(-10, -9.02) * mm});
            skLineSegment(sketch, "E283", {"start": v(-10, -10) * mm, "end": v(-10, -9.84) * mm});
            skArc(sketch, "E284", {"start": v(-1.78, 9.84) * mm, "mid": v(-3.08, 9.51) * mm, "end": v(-4.32, 9.02) * mm});
            skArc(sketch, "E285", {"start": v(-5.72, 8.2) * mm, "mid": v(-6.25, 7.8) * mm, "end": v(-6.75, 7.38) * mm});
            skArc(sketch, "E286", {"start": v(-7.55, 6.56) * mm, "mid": v(-7.88, 6.16) * mm, "end": v(-8.19, 5.74) * mm});
            skArc(sketch, "E287", {"start": v(-8.7, 4.92) * mm, "mid": v(-8.92, 4.51) * mm, "end": v(-9.12, 4.1) * mm});
            skArc(sketch, "E288", {"start": v(-9.45, 3.28) * mm, "mid": v(-9.58, 2.87) * mm, "end": v(-9.7, 2.46) * mm});
            skArc(sketch, "E289", {"start": v(-9.86, 1.64) * mm, "mid": v(-9.92, 1.23) * mm, "end": v(-9.97, 0.82) * mm});
            skArc(sketch, "E290", {"start": v(-10, 0) * mm, "mid": v(-10, -0.41) * mm, "end": v(-9.97, -0.82) * mm});
            skArc(sketch, "E291", {"start": v(-9.7, -2.46) * mm, "mid": v(-9.58, -2.87) * mm, "end": v(-9.45, -3.28) * mm});
            skArc(sketch, "E292", {"start": v(-9.12, -4.1) * mm, "mid": v(-8.92, -4.51) * mm, "end": v(-8.7, -4.92) * mm});
            skArc(sketch, "E293", {"start": v(-8.19, -5.74) * mm, "mid": v(-7.88, -6.16) * mm, "end": v(-7.55, -6.56) * mm});
            skArc(sketch, "E294", {"start": v(-6.75, -7.38) * mm, "mid": v(-6.25, -7.8) * mm, "end": v(-5.72, -8.2) * mm});
            skArc(sketch, "E295", {"start": v(-4.32, -9.02) * mm, "mid": v(-3.08, -9.51) * mm, "end": v(-1.78, -9.84) * mm});
            skArc(sketch, "E296", {"start": v(1.78, -9.84) * mm, "mid": v(3.08, -9.51) * mm, "end": v(4.32, -9.02) * mm});
            skArc(sketch, "E297", {"start": v(5.72, -8.2) * mm, "mid": v(6.25, -7.8) * mm, "end": v(6.75, -7.38) * mm});
            skArc(sketch, "E298", {"start": v(7.55, -6.56) * mm, "mid": v(7.88, -6.16) * mm, "end": v(8.19, -5.74) * mm});
            skArc(sketch, "E299", {"start": v(8.7, -4.92) * mm, "mid": v(8.92, -4.51) * mm, "end": v(9.12, -4.1) * mm});
            skArc(sketch, "E300", {"start": v(9.45, -3.28) * mm, "mid": v(9.58, -2.87) * mm, "end": v(9.7, -2.46) * mm});
            skArc(sketch, "E301", {"start": v(9.86, -1.64) * mm, "mid": v(9.92, -1.23) * mm, "end": v(9.97, -0.82) * mm});
            skArc(sketch, "E302", {"start": v(10, 0) * mm, "mid": v(10, 0.41) * mm, "end": v(9.97, 0.82) * mm});
            skArc(sketch, "E303", {"start": v(9.86, 1.64) * mm, "mid": v(9.79, 2.05) * mm, "end": v(9.7, 2.46) * mm});
            skArc(sketch, "E304", {"start": v(9.45, 3.28) * mm, "mid": v(9.3, 3.7) * mm, "end": v(9.12, 4.1) * mm});
            skArc(sketch, "E305", {"start": v(8.7, 4.92) * mm, "mid": v(8.46, 5.34) * mm, "end": v(8.19, 5.74) * mm});
            skArc(sketch, "E306", {"start": v(7.55, 6.56) * mm, "mid": v(7.16, 6.98) * mm, "end": v(6.75, 7.38) * mm});
            skArc(sketch, "E307", {"start": v(5.72, 8.2) * mm, "mid": v(5.04, 8.64) * mm, "end": v(4.32, 9.02) * mm});
            skCircle(sketch, "E308", {"center": v(0, 0) * mm, "radius": 10 * mm});
            skArc(sketch, "E309", {"start": v(-4.32, -9.02) * mm, "mid": v(-5.04, -8.64) * mm, "end": v(-5.72, -8.2) * mm});
            skArc(sketch, "E310", {"start": v(-6.75, -7.38) * mm, "mid": v(-7.16, -6.98) * mm, "end": v(-7.55, -6.56) * mm});
            skArc(sketch, "E311", {"start": v(-8.19, -5.74) * mm, "mid": v(-8.46, -5.34) * mm, "end": v(-8.7, -4.92) * mm});
            skArc(sketch, "E312", {"start": v(-9.12, -4.1) * mm, "mid": v(-9.3, -3.7) * mm, "end": v(-9.45, -3.28) * mm});
            skArc(sketch, "E313", {"start": v(-9.7, -2.46) * mm, "mid": v(-9.79, -2.05) * mm, "end": v(-9.86, -1.64) * mm});
            skSolve(sketch);
        }
        {
            var Q0;
            Q0=qCreatedBy(makeId("Right.planeOp"),FACE);
            var sketch = newSketch(context, id + "F10", { "sketchPlane" : qUnion([Q0])});
            skCircle(sketch, "E314", {"center": v(10, 0.61) * mm, "radius": 0.2 * mm});
            skSolve(sketch);
        }
        {
            var Q0;
            Q0=sQuery(id+"F9.wireOp",EDGE,"E186");
            var Q1;
            Q1=sQuery(id+"F9.wireOp",VERTEX,"E186.start");
            cPlane(context, id + "F11", {"entities" : qUnion([Q0, Q1]), "cplaneType" : CPlaneType.LINE_POINT, "offset" : 25 * mm, "width" : 150 * mm, "height" : 150 * mm});
        }
        {
            var Q0;
            Q0=qCreatedBy(id+"F11.planeOp",FACE);
            var sketch = newSketch(context, id + "F12", { "sketchPlane" : qUnion([Q0])});
            skCircle(sketch, "E315", {"center": v(-9.84, 0.61) * mm, "radius": 0.2 * mm});
            skSolve(sketch);
        }
        {
            var Q0;
            Q0=makeQuery(id+"F12.imprint","IMPRINT",FACE,{"disambiguationData":[TD([[makeQuery(id+"F12.imprint","IMPRINT",EDGE,{"derivedFrom":sQuery(id+"F12.wireOp",EDGE,"E315")}),1.0]])]});
            var Q1;
            Q1=sQuery(id+"F12.wireOp",EDGE,"E315");
            var Q2;
            Q2=sQuery(id+"F9.wireOp",EDGE,"E186");
            var Q3;
            Q3=sQuery(id+"F9.wireOp",EDGE,"E284");
            var Q4;
            Q4=sQuery(id+"F9.wireOp",EDGE,"E190");
            var Q5;
            Q5=sQuery(id+"F9.wireOp",EDGE,"E307");
            var Q6;
            Q6=sQuery(id+"F9.wireOp",EDGE,"E194");
            var Q7;
            Q7=sQuery(id+"F9.wireOp",EDGE,"E285");
            var Q8;
            Q8=sQuery(id+"F9.wireOp",EDGE,"E198");
            var Q9;
            Q9=sQuery(id+"F9.wireOp",EDGE,"E306");
            var Q10;
            Q10=sQuery(id+"F9.wireOp",EDGE,"E202");
            var Q11;
            Q11=sQuery(id+"F9.wireOp",EDGE,"E286");
            var Q12;
            Q12=sQuery(id+"F9.wireOp",EDGE,"E206");
            var Q13;
            Q13=sQuery(id+"F9.wireOp",EDGE,"E305");
            var Q14;
            Q14=sQuery(id+"F9.wireOp",EDGE,"E210");
            var Q15;
            Q15=sQuery(id+"F9.wireOp",EDGE,"E287");
            var Q16;
            Q16=sQuery(id+"F9.wireOp",EDGE,"E214");
            var Q17;
            Q17=sQuery(id+"F9.wireOp",EDGE,"E218");
            var Q18;
            Q18=sQuery(id+"F9.wireOp",EDGE,"E304");
            var Q19;
            Q19=sQuery(id+"F9.wireOp",EDGE,"E303");
            var Q20;
            Q20=sQuery(id+"F9.wireOp",EDGE,"E222");
            var Q21;
            Q21=sQuery(id+"F9.wireOp",EDGE,"E226");
            var Q22;
            Q22=sQuery(id+"F9.wireOp",EDGE,"E230");
            var Q23;
            Q23=sQuery(id+"F9.wireOp",EDGE,"E302");
            var Q24;
            Q24=sQuery(id+"F9.wireOp",EDGE,"E233");
            var Q25;
            Q25=sQuery(id+"F9.wireOp",EDGE,"E236");
            var Q26;
            Q26=sQuery(id+"F9.wireOp",EDGE,"E301");
            var Q27;
            Q27=sQuery(id+"F9.wireOp",EDGE,"E240");
            var Q28;
            Q28=sQuery(id+"F9.wireOp",EDGE,"E244");
            var Q29;
            Q29=sQuery(id+"F9.wireOp",EDGE,"E300");
            var Q30;
            Q30=sQuery(id+"F9.wireOp",EDGE,"E248");
            var Q31;
            Q31=sQuery(id+"F9.wireOp",EDGE,"E252");
            var Q32;
            Q32=sQuery(id+"F9.wireOp",EDGE,"E299");
            var Q33;
            Q33=sQuery(id+"F9.wireOp",EDGE,"E256");
            var Q34;
            Q34=sQuery(id+"F9.wireOp",EDGE,"E260");
            var Q35;
            Q35=sQuery(id+"F9.wireOp",EDGE,"E298");
            var Q36;
            Q36=sQuery(id+"F9.wireOp",EDGE,"E264");
            var Q37;
            Q37=sQuery(id+"F9.wireOp",EDGE,"E268");
            var Q38;
            Q38=sQuery(id+"F9.wireOp",EDGE,"E297");
            var Q39;
            Q39=sQuery(id+"F9.wireOp",EDGE,"E272");
            var Q40;
            Q40=sQuery(id+"F9.wireOp",EDGE,"E276");
            var Q41;
            Q41=sQuery(id+"F9.wireOp",EDGE,"E296");
            var Q42;
            Q42=sQuery(id+"F9.wireOp",EDGE,"E280");
            var Q43;
            Q43=sQuery(id+"F9.wireOp",EDGE,"E309");
            var Q44;
            Q44=sQuery(id+"F9.wireOp",EDGE,"E310");
            var Q45;
            Q45=sQuery(id+"F9.wireOp",EDGE,"E311");
            var Q46;
            Q46=sQuery(id+"F9.wireOp",EDGE,"E312");
            var Q47;
            Q47=sQuery(id+"F9.wireOp",EDGE,"E313");
            var Q48;
            Q48=sQuery(id+"F9.wireOp",EDGE,"E290");
            var Q49;
            Q49=sQuery(id+"F9.wireOp",EDGE,"E289");
            var Q50;
            Q50=sQuery(id+"F9.wireOp",EDGE,"E288");
            sweep(context, id + "F13", {"profiles" : qUnion([Q0]), "surfaceProfiles" : qUnion([Q1]), "path" : qUnion([Q2, Q3, Q4, Q5, Q6, Q7, Q8, Q9, Q10, Q11, Q12, Q13, Q14, Q15, Q16, Q17, Q18, Q19, Q20, Q21, Q22, Q23, Q24, Q25, Q26, Q27, Q28, Q29, Q30, Q31, Q32, Q33, Q34, Q35, Q36, Q37, Q38, Q39, Q40, Q41, Q42, Q43, Q44, Q45, Q46, Q47, Q48, Q49, Q50])});
        }
        {
            var Q0;
            Q0=makeQuery(id+"F10.imprint","IMPRINT",FACE,{"disambiguationData":[TD([[makeQuery(id+"F10.imprint","IMPRINT",EDGE,{"derivedFrom":sQuery(id+"F10.wireOp",EDGE,"E314")}),1.0]])]});
            var Q1;
            Q1=sQuery(id+"F10.wireOp",EDGE,"E314");
            var Q2;
            Q2=sQuery(id+"F9.wireOp",EDGE,"E308");
            sweep(context, id + "F14", {"profiles" : qUnion([Q0]), "surfaceProfiles" : qUnion([Q1]), "path" : qUnion([Q2])});
        }
    });
